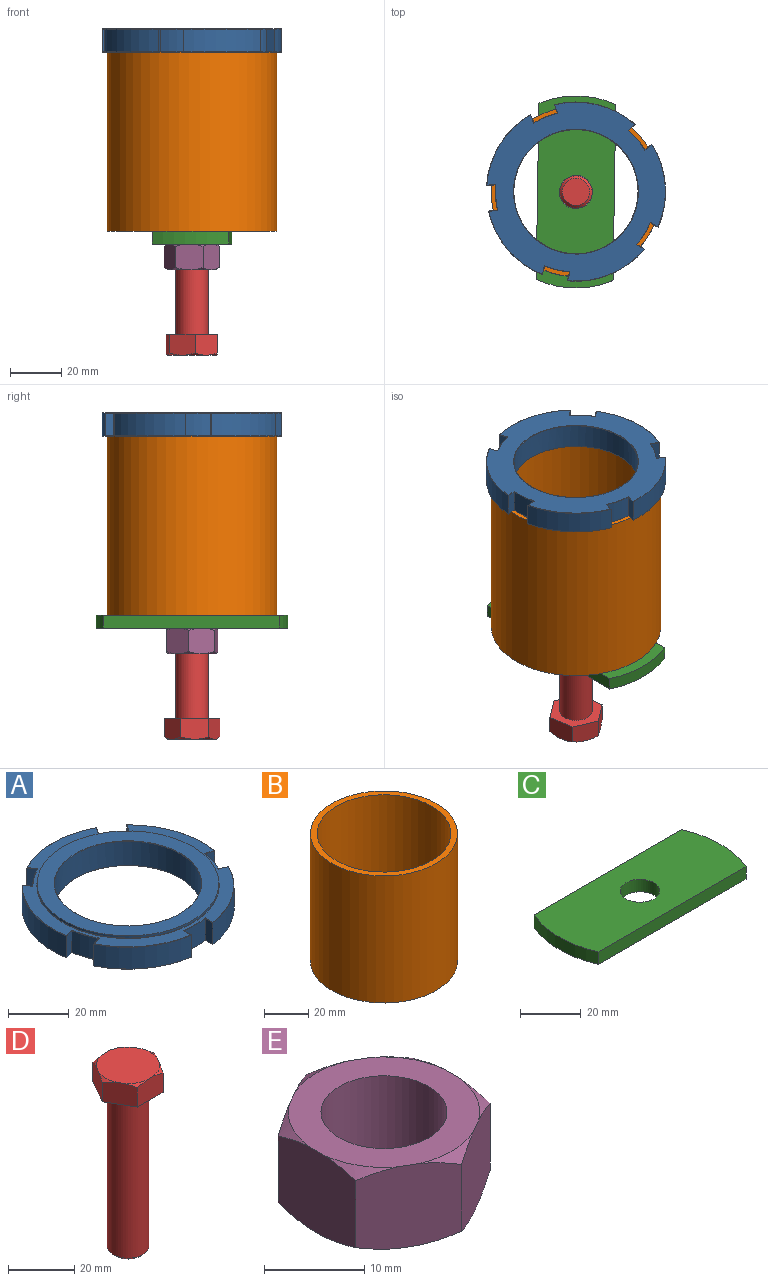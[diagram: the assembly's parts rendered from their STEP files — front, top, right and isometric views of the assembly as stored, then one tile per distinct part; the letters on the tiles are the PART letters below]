
ASSEMBLY  parts=5 mates=7
PART A: 69 faces, bbox 70x69.6x10 mm
  f0: plane 60x60mm, normal (0,0,1), area 964.7mm2, adj f23,f25
  f1: cylinder r=35mm len=31.04mm, axis (0,0,-1), area 298.7mm2, adj f15,f19,f46,f67
  f2: cylinder r=35mm len=32.63mm, axis (0,0,-1), area 298.7mm2, adj f12,f16,f38,f59
  f3: cylinder r=35mm len=31.04mm, axis (0,0,-1), area 298.7mm2, adj f9,f13,f30,f51
  f4: cylinder r=35mm len=26.4mm, axis (0,0,-1), area 298.7mm2, adj f6,f10,f31,f52
  f5: cylinder r=35mm len=26.4mm, axis (0,0,-1), area 298.7mm2, adj f7,f18,f39,f60
  f6: plane 8.8x3.54mm, normal (-1,0,0), area 31.2mm2, adj f4,f8,f33,f54
  f7: plane 8.8x3.54mm, normal (1,0,0), area 31.2mm2, adj f5,f8,f37,f58
  f8: cylinder r=31.5mm len=10mm, axis (0,0,-1), area 88.4mm2, adj f6,f7,f35,f56
  f9: plane 8.8x3.37mm, normal (-0.31,-0.95,0), area 31.2mm2, adj f3,f11,f28,f49
  f10: plane 8.8x3.37mm, normal (0.31,0.95,0), area 31.2mm2, adj f4,f11,f29,f50
  f11: cylinder r=31.5mm len=9.51mm, axis (0,0,-1), area 88.4mm2, adj f9,f10,f27,f48
  f12: plane 8.8x2.86mm, normal (0.81,-0.59,0), area 31.2mm2, adj f2,f14,f36,f57
  f13: plane 8.8x2.86mm, normal (-0.81,0.59,0), area 31.2mm2, adj f3,f14,f32,f53
  f14: cylinder r=31.5mm len=8.8mm, axis (0,0,-1), area 88.4mm2, adj f12,f13,f34,f55
  f15: plane 8.8x2.86mm, normal (0.81,0.59,0), area 31.2mm2, adj f1,f17,f44,f65
  f16: plane 8.8x2.86mm, normal (-0.81,-0.59,0), area 31.2mm2, adj f2,f17,f40,f61
  f17: cylinder r=31.5mm len=8.8mm, axis (0,0,-1), area 88.4mm2, adj f15,f16,f42,f63
  f18: plane 8.8x3.37mm, normal (-0.31,0.95,0), area 31.2mm2, adj f5,f20,f41,f62
  f19: plane 8.8x3.37mm, normal (0.31,-0.95,0), area 31.2mm2, adj f1,f20,f45,f66
  f20: cylinder r=31.5mm len=9.51mm, axis (0,0,-1), area 88.4mm2, adj f18,f19,f43,f64
  f21: plane 69.8x69.43mm, normal (0,0,-1), area 1778.2mm2, adj f27,f28,f29,f30,f31,f32,f33,f34
  f22: cylinder r=24.25mm len=48.5mm, axis (0,0,1), area 1493.2mm2, adj f23,f24
  f23: cone r=24.25mm half-angle=45deg, axis (0,0,1), area 21.6mm2, adj f0,f22
  f24: cone r=24.25mm half-angle=45deg, axis (0,0,-1), area 15.3mm2, adj f22,f47
  f25: cylinder r=30mm len=60mm, axis (0,0,1), area 169.6mm2, adj f0,f68
  f26: plane 69.8x69.43mm, normal (0,0,1), area 801mm2, adj f48,f49,f50,f51,f52,f53,f54,f55
  f27: cone r=31.4mm half-angle=45deg, axis (0,0,1), area 1.4mm2, adj f11,f21,f28,f29
  f28: plane 3.45x1.23mm, normal (-0.22,-0.67,-0.71), area 0.5mm2, adj f9,f21,f27,f30
  f29: plane 3.51x1.15mm, normal (0.22,0.67,-0.71), area 0.5mm2, adj f10,f21,f27,f31
  f30: cone r=35mm half-angle=45deg, axis (0,0,1), area 4.8mm2, adj f3,f21,f28,f32
  f31: cone r=35mm half-angle=45deg, axis (0,0,1), area 4.8mm2, adj f4,f21,f29,f33
  f32: plane 3.02x2.09mm, normal (-0.57,0.42,-0.71), area 0.5mm2, adj f13,f21,f30,f34
  f33: plane 3.66x0.1mm, normal (-0.71,0,-0.71), area 0.5mm2, adj f6,f21,f31,f35
  f34: cone r=31.4mm half-angle=45deg, axis (0,0,1), area 1.4mm2, adj f14,f21,f32,f36
  f35: cone r=31.4mm half-angle=45deg, axis (0,0,1), area 1.4mm2, adj f8,f21,f33,f37
  f36: plane 2.9x2.23mm, normal (0.57,-0.42,-0.71), area 0.5mm2, adj f12,f21,f34,f38
  f37: plane 3.66x0.1mm, normal (0.71,0,-0.71), area 0.5mm2, adj f7,f21,f35,f39
  f38: cone r=35mm half-angle=45deg, axis (0,0,1), area 4.8mm2, adj f2,f21,f36,f40
  f39: cone r=35mm half-angle=45deg, axis (0,0,1), area 4.8mm2, adj f5,f21,f37,f41
  f40: plane 2.9x2.23mm, normal (-0.57,-0.42,-0.71), area 0.5mm2, adj f16,f21,f38,f42
  f41: plane 3.51x1.15mm, normal (-0.22,0.67,-0.71), area 0.5mm2, adj f18,f21,f39,f43
  f42: cone r=31.4mm half-angle=45deg, axis (0,0,1), area 1.4mm2, adj f17,f21,f40,f44
  f43: cone r=31.4mm half-angle=45deg, axis (0,0,1), area 1.4mm2, adj f20,f21,f41,f45
  f44: plane 3.02x2.09mm, normal (0.57,0.42,-0.71), area 0.5mm2, adj f15,f21,f42,f46
  f45: plane 3.45x1.23mm, normal (0.22,-0.67,-0.71), area 0.5mm2, adj f19,f21,f43,f46
  f46: cone r=35mm half-angle=45deg, axis (0,0,1), area 4.8mm2, adj f1,f21,f44,f45
  f47: cone r=24.39mm half-angle=67.5deg, axis (0,0,-1), area 11.7mm2, adj f21,f24
  f48: cone r=31.5mm half-angle=45deg, axis (0,0,-1), area 1.4mm2, adj f11,f26,f49,f50
  f49: plane 3.45x1.23mm, normal (-0.22,-0.67,0.71), area 0.5mm2, adj f9,f26,f48,f51
  f50: plane 3.51x1.15mm, normal (0.22,0.67,0.71), area 0.5mm2, adj f10,f26,f48,f52
  f51: cone r=34.9mm half-angle=45deg, axis (0,0,-1), area 4.8mm2, adj f3,f26,f49,f53
  f52: cone r=34.9mm half-angle=45deg, axis (0,0,-1), area 4.8mm2, adj f4,f26,f50,f54
  f53: plane 3.02x2.09mm, normal (-0.57,0.42,0.71), area 0.5mm2, adj f13,f26,f51,f55
  f54: plane 3.66x0.1mm, normal (-0.71,0,0.71), area 0.5mm2, adj f6,f26,f52,f56
  f55: cone r=31.5mm half-angle=45deg, axis (0,0,-1), area 1.4mm2, adj f14,f26,f53,f57
  f56: cone r=31.5mm half-angle=45deg, axis (0,0,-1), area 1.4mm2, adj f8,f26,f54,f58
  f57: plane 2.9x2.23mm, normal (0.57,-0.42,0.71), area 0.5mm2, adj f12,f26,f55,f59
  f58: plane 3.66x0.1mm, normal (0.71,0,0.71), area 0.5mm2, adj f7,f26,f56,f60
  f59: cone r=34.9mm half-angle=45deg, axis (0,0,-1), area 4.8mm2, adj f2,f26,f57,f61
  f60: cone r=34.9mm half-angle=45deg, axis (0,0,-1), area 4.8mm2, adj f5,f26,f58,f62
  f61: plane 2.9x2.23mm, normal (-0.57,-0.42,0.71), area 0.5mm2, adj f16,f26,f59,f63
  f62: plane 3.51x1.15mm, normal (-0.22,0.67,0.71), area 0.5mm2, adj f18,f26,f60,f64
  f63: cone r=31.5mm half-angle=45deg, axis (0,0,-1), area 1.4mm2, adj f17,f26,f61,f65
  f64: cone r=31.5mm half-angle=45deg, axis (0,0,-1), area 1.4mm2, adj f20,f26,f62,f66
  f65: plane 3.02x2.09mm, normal (0.57,0.42,0.71), area 0.5mm2, adj f15,f26,f63,f67
  f66: plane 3.45x1.23mm, normal (0.22,-0.67,0.71), area 0.5mm2, adj f19,f26,f64,f67
  f67: cone r=34.9mm half-angle=45deg, axis (0,0,-1), area 4.8mm2, adj f1,f26,f65,f66
  f68: cone r=30mm half-angle=45deg, axis (0,0,-1), area 26.7mm2, adj f25,f26
PART B: 4 faces, bbox 66.2x66.2x70 mm
  f0: cylinder r=30.1mm len=70mm, axis (0,0,-1), area 13238.7mm2, adj f2,f3
  f1: cylinder r=33.1mm len=70mm, axis (0,0,-1), area 14558.1mm2, adj f2,f3
  f2: plane 66.2x66.2mm, normal (0,0,1), area 595.6mm2, adj f0,f1
  f3: plane 66.2x66.2mm, normal (0,0,-1), area 595.6mm2, adj f0,f1
PART C: 7 faces, bbox 75x30x5 mm
  f0: plane 68.74x5mm, normal (0,1,0), area 343.7mm2, adj f1,f3,f4,f5
  f1: cylinder r=37.5mm len=30mm, axis (0,0,1), area 154.3mm2, adj f0,f2,f4,f5
  f2: plane 68.74x5mm, normal (0,-1,0), area 343.7mm2, adj f1,f3,f4,f5
  f3: cylinder r=37.5mm len=30mm, axis (0,0,1), area 154.3mm2, adj f0,f2,f4,f5
  f4: plane 75x30mm, normal (0,0,1), area 2055.7mm2, adj f0,f1,f2,f3,f6
  f5: plane 75x30mm, normal (0,0,-1), area 2055.7mm2, adj f0,f1,f2,f3,f6
  f6: cylinder r=6.5mm len=13mm, axis (0,0,-1), area 204.2mm2, adj f4,f5
PART D: 17 faces, bbox 21.9x21.8x68 mm
  f0: plane 10.98x8mm, normal (0,-1,0), area 84.6mm2, adj f1,f5,f6,f10,f12,f16
  f1: plane 9.51x8mm, normal (0.87,-0.5,0), area 84.6mm2, adj f0,f2,f6,f10,f15,f16
  f2: plane 9.51x8mm, normal (0.87,0.5,0), area 84.6mm2, adj f1,f3,f6,f10,f14,f15
  f3: plane 10.98x8mm, normal (0,1,0), area 84.6mm2, adj f2,f4,f6,f10,f13,f14
  f4: plane 9.51x8mm, normal (-0.87,0.5,0), area 84.6mm2, adj f3,f5,f6,f10,f11,f13
  f5: plane 9.51x8mm, normal (-0.87,-0.5,0), area 84.6mm2, adj f0,f4,f6,f10,f11,f12
  f6: plane 19.14x19mm, normal (0,0,1), area 287.1mm2, adj f0,f1,f2,f3,f4,f5,f11,f12
  f7: cylinder r=6.3mm len=59mm, axis (0,0,-1), area 2335.5mm2, adj f9,f10
  f8: plane 10.6x10.6mm, normal (0,0,-1), area 88.2mm2, adj f9
  f9: cone r=6.3mm half-angle=45deg, axis (0,0,1), area 51.5mm2, adj f7,f8
  f10: plane 21.94x19mm, normal (0,0,-1), area 187.9mm2, adj f0,f1,f2,f3,f4,f5,f7
  f11: cone r=9.57mm half-angle=57.3deg, axis (0,0,-1), area 5.1mm2, adj f4,f5,f6
  f12: cone r=9.57mm half-angle=57.3deg, axis (0,0,-1), area 5.1mm2, adj f0,f5,f6
  f13: cone r=9.57mm half-angle=57.3deg, axis (0,0,-1), area 5.1mm2, adj f3,f4,f6
  f14: cone r=9.57mm half-angle=57.3deg, axis (0,0,-1), area 5.1mm2, adj f2,f3,f6
  f15: cone r=9.57mm half-angle=57.3deg, axis (0,0,-1), area 5.1mm2, adj f1,f2,f6
  f16: cone r=9.57mm half-angle=57.3deg, axis (0,0,-1), area 5.1mm2, adj f0,f1,f6
PART E: 21 faces, bbox 21.8x21.9x10 mm
  f0: plane 10.01x9.51mm, normal (-0.5,-0.87,0), area 103.4mm2, adj f1,f5,f6,f7,f10,f14,f15,f20
  f1: plane 10.01x9.51mm, normal (0.5,-0.87,0), area 103.4mm2, adj f0,f2,f6,f7,f13,f14,f19,f20
  f2: plane 10.98x10.01mm, normal (1,0,0), area 103.4mm2, adj f1,f3,f6,f7,f12,f13,f18,f19
  f3: plane 10.01x9.51mm, normal (0.5,0.87,0), area 103.4mm2, adj f2,f4,f6,f7,f11,f12,f17,f18
  f4: plane 10.01x9.51mm, normal (-0.5,0.87,0), area 103.4mm2, adj f3,f5,f6,f7,f9,f11,f16,f17
  f5: plane 10.98x10.01mm, normal (-1,0,0), area 103.4mm2, adj f0,f4,f6,f7,f9,f10,f15,f16
  f6: plane 19.14x19mm, normal (0,0,-1), area 162.4mm2, adj f0,f1,f2,f3,f4,f5,f8,f15
  f7: plane 19.14x19mm, normal (0,0,1), area 162.4mm2, adj f0,f1,f2,f3,f4,f5,f8,f9
  f8: cylinder r=6.3mm len=12.6mm, axis (0,0,1), area 395.8mm2, adj f6,f7
  f9: cone r=9.57mm half-angle=57.3deg, axis (0,0,-1), area 5.1mm2, adj f4,f5,f7
  f10: cone r=9.57mm half-angle=57.3deg, axis (0,0,-1), area 5.1mm2, adj f0,f5,f7
  f11: cone r=9.57mm half-angle=57.3deg, axis (0,0,-1), area 5.1mm2, adj f3,f4,f7
  f12: cone r=9.57mm half-angle=57.3deg, axis (0,0,-1), area 5.1mm2, adj f2,f3,f7
  f13: cone r=9.57mm half-angle=57.3deg, axis (0,0,-1), area 5.1mm2, adj f1,f2,f7
  f14: cone r=9.57mm half-angle=57.3deg, axis (0,0,-1), area 5.1mm2, adj f0,f1,f7
  f15: cone r=9.57mm half-angle=57.3deg, axis (0,0,1), area 5.1mm2, adj f0,f5,f6
  f16: cone r=9.57mm half-angle=57.3deg, axis (0,0,1), area 5.1mm2, adj f4,f5,f6
  f17: cone r=9.57mm half-angle=57.3deg, axis (0,0,1), area 5.1mm2, adj f3,f4,f6
  f18: cone r=9.57mm half-angle=57.3deg, axis (0,0,1), area 5.1mm2, adj f2,f3,f6
  f19: cone r=9.57mm half-angle=57.3deg, axis (0,0,1), area 5.1mm2, adj f1,f2,f6
  f20: cone r=9.57mm half-angle=57.3deg, axis (0,0,1), area 5.1mm2, adj f0,f1,f6
PLACE A rot(axis=(0.98,0.19,0),180deg) t=(0,0,39)mm
PLACE B at identity fixed
PLACE C rot(axis=(0,0,1),89.1deg) t=(0,0,-40)mm
PLACE D rot(axis=(0.95,0.32,0),180deg) t=(0,0,-45.31)mm
PLACE E rot(axis=(0,0,1),23.3deg) t=(0,0,-45)mm
MATE planar E.f7 <-> C.f1  axis (0,0,1) through (-6.93,6.6,-40)mm
MATE cylindrical C.f1 <-> E.f8  axis (0,0,-1) through (0,0,-37.5)mm
MATE planar C.f4 <-> B.f1  axis (0,0,1) through (-15.53,-34.13,-35)mm
MATE cylindrical A.f1 <-> B.f0  axis (0,0,-1) through (0,0,34.45)mm
MATE cylindrical C.f1 <-> B.f1  axis (0,0,1) through (0,0,-37.5)mm
MATE cylindrical D.f7 <-> E.f8  axis (0,0,1) through (0,0,-45.81)mm
MATE planar A.f26 <-> B.f1  axis (0,0,-1) through (-2.39,-31.31,35)mm
